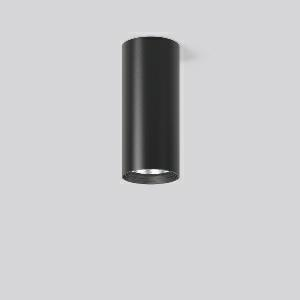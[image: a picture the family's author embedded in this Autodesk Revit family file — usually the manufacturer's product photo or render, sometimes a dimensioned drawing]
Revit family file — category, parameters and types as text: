
# Revit family: heledon_mini_a_931209_003_3_6f1e
name_source: partatom
category: Lighting Fixtures
units: mm (PartAtom-declared; Revit-internal decimal feet)

## family parameters
Cut with Voids When Loaded = No
Host = Face
Light Source = No
Part Type = Normal
Room Calculation Point = No
Round Connector Dimension = Use Diameter
Shared = No

## types (1)
- HELEDON mini A (1 x LED Modul 935, 3600 lm, 3500)
    Apparent Load = 29 VA
    Approval mark = CE
    CIE Flux Codes = 99 100 100 100 100
    Color Rendering = 92
    Color Temperature = 3500
    Default Elevation = 1800 mm
    Description = Series: HELEDON mini
Cylindrical surface-mounted downlight. Housing: die-cast aluminium, powder-coated. Internal ceiling frame polycarbonate with bayonet mounting. Black plastic ring and recessed LED to prevent glare from the side. Optical assembly with reflector made of MIRO-Silver with 98% total light reflection for outstanding efficiency - can be changed without tools. Best colour rendering index Ra>90. Suitable for Ceiling mounting. Easy installation with a separate ceiling frame with bayonet mounting and plug connection. Driver integrated. Connected via plug-in connector. High quality converter without flickering and stroboscopic effect. The following accessories can be mounted without use of tools: interchangeable lenses, decorative glasses, honeycomb louvre, clear and frosted diffusers, white interchangeable plastic ring. 
Colour: deep black, matt (RAL 9005)
Diameter: 87 mm
Height: 197 mm
Lamp: LED
Socket: without socket
Colour temperature: 3500K
Colour rendering index (CRI): 92
System power: 29 W
Rated luminous flux: 3600 lm
Luminous efficiency: 124 lm/W
Control gear: Regulated power supply
Protection class: I
Type of protection: IP 20
    Height = 197 mm
    Lamp = 1 x LED Modul 935
    Lamp Light Flux = 3600 lm
    Lamp count = 1
    Length = 87 mm
    Lifetime = 50000 h
    Luminous efficacy = 124 lm/W
    Manufacturer = RZB
    ModVariant = No
    Model = 931209.003.3
    Mounting Place = Ceiling
    Mounting Type = Surface mounted
    Number of Poles = 1
    OnlyDefault = Yes
    Power Factor = 1
    Product Name = HELEDON mini A
    Product group = Surface mounted downlights
    ProductGroupID = 302
    Protection Class = Protection class I
    Protection Degree = IP 20
    RLX_Detail_Level = 1
    RLX_Emergency_Light_Flux = 0 lm
    RLX_Emergency_Type = 0
    RLX_Emergency_Type_DB = No
    RlxData = <blob elided: 106289 chars, md5=53e1efd5>
    Socket = socket
    Standby Power = 0 W
    System Light Flux = 3600 lm
    System Power = 29 W
    Type Comments = Product without accessories
    Type Image = 931188.003.jpg
    URL = http://relux.com
    VarID = ---
    Voltage = 230 V
    Voltage Range = 220-240 V
    Weight = 0.00 kg
    Width = 0 mm  [stored 0 ft]

note: [stored X ft] marks values corroborated as IEEE doubles in the binary element streams (Revit-internal decimal feet)

## geometry (parser evidence)
native form markers: Blend x4, Sweep x10
no freeform markers — native parametric forms only
